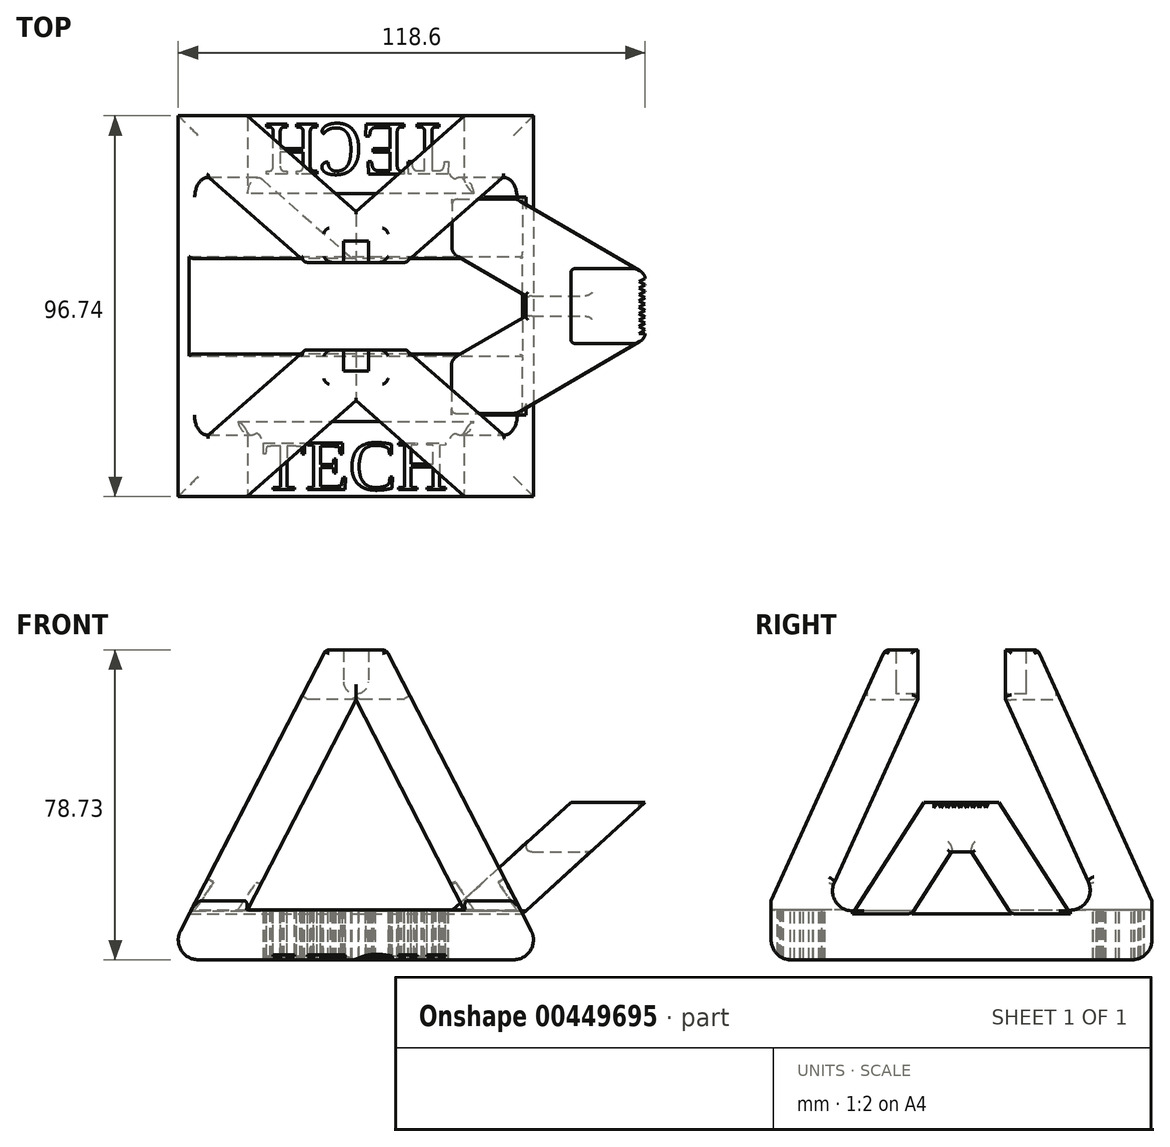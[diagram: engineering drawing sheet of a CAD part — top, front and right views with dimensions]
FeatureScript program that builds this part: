
annotation { "Feature Type Name" : "Feature", "Feature Type Description" : "" }
export const myFeature = defineFeature(function(context is Context, id is Id, definition is map)
    precondition{}
    {
        {
            var Q0;
            Q0=qCreatedBy(makeId("Front.planeOp"),FACE);
            var sketch = newSketch(context, id + "F0", { "sketchPlane" : qUnion([Q0])});
            skLineSegment(sketch, "E0", {"start": v(0, 54.73) * mm, "end": v(0, -72.39) * mm, "construction": true});
            skLineSegment(sketch, "E1", {"start": v(0, 35.91) * mm, "end": v(-7.58, 35.91) * mm});
            skLineSegment(sketch, "E2", {"start": v(-7.58, 35.91) * mm, "end": v(-48.37, -43.08) * mm});
            skLineSegment(sketch, "E3", {"start": v(-48.37, -43.08) * mm, "end": v(0, -43.08) * mm});
            skLineSegment(sketch, "E4", {"start": v(0, -43.08) * mm, "end": v(0, 35.91) * mm});
            skLineSegment(sketch, "E5.MirrorCS", {"start": v(7.58, 35.91) * mm, "end": v(48.37, -43.08) * mm});
            skLineSegment(sketch, "E6.MirrorCS", {"start": v(0, 35.91) * mm, "end": v(7.58, 35.91) * mm});
            skLineSegment(sketch, "E7.MirrorCS", {"start": v(48.37, -43.08) * mm, "end": v(0, -43.08) * mm});
            skSolve(sketch);
        }
        {
            var Q0;
            Q0=makeQuery(id+"F0.imprint","IMPRINT",FACE,{"disambiguationData":[TD([[makeQuery(id+"F0.imprint","IMPRINT",EDGE,{"derivedFrom":sQuery(id+"F0.wireOp",EDGE,"E1")}),1.0]])]});
            var Q1;
            Q1=makeQuery(id+"F0.imprint","IMPRINT",FACE,{"disambiguationData":[TD([[makeQuery(id+"F0.imprint","IMPRINT",EDGE,{"derivedFrom":sQuery(id+"F0.wireOp",EDGE,"E4")}),-1.0]])]});
            extrude(context, id + "F1", {"entities" : qUnion([Q0, Q1]), "endBound" : BoundingType.SYMMETRIC, "depth" : 96.75 * mm});
        }
        {
            var Q0;
            Q0=qCreatedBy(makeId("Right.planeOp"),FACE);
            cPlane(context, id + "F2", {"entities" : qUnion([Q0]), "cplaneType" : CPlaneType.OFFSET, "offset" : 48.37 * mm, "width" : 152.4 * mm, "height" : 152.4 * mm});
        }
        {
            var Q0;
            Q0=qCreatedBy(id+"F2.planeOp",FACE);
            var sketch = newSketch(context, id + "F3", { "sketchPlane" : qUnion([Q0])});
            skLineSegment(sketch, "E8.bottom", {"start": v(49.54, -43.11) * mm, "end": v(-49.54, -43.41) * mm});
            skLineSegment(sketch, "E8.left", {"start": v(49.54, -43.11) * mm, "end": v(49.54, 35.91) * mm});
            skLineSegment(sketch, "E8.right", {"start": v(-49.54, -43.41) * mm, "end": v(-49.54, 35.91) * mm});
            skPoint(sketch, "E8.middle", {"position": v(0, 0) * mm});
            skLineSegment(sketch, "E9", {"start": v(0, 43.26) * mm, "end": v(0, -59.7) * mm, "construction": true});
            skPoint(sketch, "E9.endSnap0", {"position": v(0, -43.26) * mm});
            skLineSegment(sketch, "E10.0", {"start": v(48.25, -30.42) * mm, "end": v(-35.6, -30.67) * mm});
            skLineSegment(sketch, "E11.0", {"start": v(-11.11, 35.91) * mm, "end": v(-11.11, 23.21) * mm});
            skLineSegment(sketch, "E12.0", {"start": v(-23.81, 35.91) * mm, "end": v(-23.81, 35.65) * mm});
            skLineSegment(sketch, "E13", {"start": v(-49.54, 35.91) * mm, "end": v(49.54, 35.91) * mm});
            skPoint(sketch, "E14.orphan", {"position": v(0, 61.2) * mm});
            skPoint(sketch, "E15.orphan", {"position": v(49.54, 43.41) * mm});
            skPoint(sketch, "E16.orphan", {"position": v(-49.54, 43.11) * mm});
            skLineSegment(sketch, "E17.0", {"start": v(-48.25, 35.65) * mm, "end": v(48.25, 35.65) * mm});
            skLineSegment(sketch, "E18", {"start": v(-11.11, 23.21) * mm, "end": v(-35.6, -30.67) * mm});
            skLineSegment(sketch, "E19.0", {"start": v(-19.41, 35.65) * mm, "end": v(-49.54, -30.65) * mm});
            skLineSegment(sketch, "E20.trimOffspring", {"start": v(-11.11, 23.21) * mm, "end": v(48.25, 23.21) * mm});
            skLineSegment(sketch, "E21.trimOffspring", {"start": v(-35.55, 35.65) * mm, "end": v(-35.55, 35.91) * mm});
            skLineSegment(sketch, "E22.trimOffspring", {"start": v(-23.81, -43.33) * mm, "end": v(-23.81, -59.7) * mm});
            skLineSegment(sketch, "E23.trimOffspring", {"start": v(-11.11, -43.3) * mm, "end": v(-11.11, -59.7) * mm});
            skLineSegment(sketch, "E24.MirrorCS", {"start": v(11.11, 35.91) * mm, "end": v(11.11, 23.21) * mm});
            skLineSegment(sketch, "E25.MirrorCS", {"start": v(19.41, 35.65) * mm, "end": v(49.54, -30.65) * mm});
            skLineSegment(sketch, "E26.MirrorCS", {"start": v(11.11, 23.21) * mm, "end": v(35.6, -30.67) * mm});
            skSolve(sketch);
        }
        {
            var Q0;
            {var subQ5=sQuery(id+"F3.wireOp",EDGE,"E21.trimOffspring");Q0=makeQuery(id+"F3.imprint","IMPRINT",FACE,{"disambiguationData":[TD([[makeQuery(id+"F3.imprint","IMPRINT",EDGE,{"derivedFrom":subQ5}),1.0]])]});}
            var Q1;
            {var subQ4=sQuery(id+"F3.wireOp",EDGE,"E13");var subQ5=sQuery(id+"F3.wireOp",EDGE,"E8.left");var subQ6=makeQuery(id+"F3.imprint","INTERSECT",VERTEX,{"derivedFrom":[subQ5,subQ4]});Q1=makeQuery(id+"F3.imprint","IMPRINT",FACE,{"disambiguationData":[TD([[makeQuery(id+"F3.imprint","IMPRINT",EDGE,{"disambiguationData":[TD([[subQ6,1.0]])],"derivedFrom":subQ5}),1.0]])]});}
            var Q2;
            {var subQ0=sQuery(id+"F3.wireOp",EDGE,"E13");var subQ1=sQuery(id+"F3.wireOp",EDGE,"E11.0");var subQ2=makeQuery(id+"F3.imprint","INTERSECT",VERTEX,{"derivedFrom":[subQ1,subQ0]});Q2=makeQuery(id+"F3.imprint","IMPRINT",FACE,{"disambiguationData":[TD([[makeQuery(id+"F3.imprint","IMPRINT",EDGE,{"disambiguationData":[TD([[subQ2,-1.0]])],"derivedFrom":subQ1}),1.0]])]});}
            var Q3;
            {var subQ0=sQuery(id+"F3.wireOp",EDGE,"E12.0");Q3=makeQuery(id+"F3.imprint","IMPRINT",FACE,{"disambiguationData":[TD([[makeQuery(id+"F3.imprint","IMPRINT",EDGE,{"derivedFrom":subQ0}),-1.0]])]});}
            var Q4;
            {var subQ0=sQuery(id+"F3.wireOp",EDGE,"E12.0");Q4=makeQuery(id+"F3.imprint","IMPRINT",FACE,{"disambiguationData":[TD([[makeQuery(id+"F3.imprint","IMPRINT",EDGE,{"derivedFrom":subQ0}),1.0]])]});}
            var Q5;
            {var subQ0=sQuery(id+"F3.wireOp",EDGE,"E17.0");var subQ1=sQuery(id+"F3.wireOp",EDGE,"E8.left");var subQ2=makeQuery(id+"F3.imprint","INTERSECT",VERTEX,{"derivedFrom":[subQ1,subQ0]});Q5=makeQuery(id+"F3.imprint","IMPRINT",FACE,{"disambiguationData":[TD([[makeQuery(id+"F3.imprint","IMPRINT",EDGE,{"disambiguationData":[TD([[subQ2,1.0]])],"derivedFrom":subQ1}),1.0]])]});}
            var Q6;
            {var subQ0=sQuery(id+"F3.wireOp",EDGE,"E20.trimOffspring");var subQ1=sQuery(id+"F3.wireOp",EDGE,"E8.left");var subQ2=makeQuery(id+"F3.imprint","INTERSECT",VERTEX,{"derivedFrom":[subQ1,subQ0]});Q6=makeQuery(id+"F3.imprint","IMPRINT",FACE,{"disambiguationData":[TD([[makeQuery(id+"F3.imprint","IMPRINT",EDGE,{"disambiguationData":[TD([[subQ2,1.0]])],"derivedFrom":subQ1}),1.0]])]});}
            var Q7;
            {var subQ1=sQuery(id+"F3.wireOp",EDGE,"E11.0");var subQ3=sQuery(id+"F3.wireOp",EDGE,"E17.0");var subQ4=makeQuery(id+"F3.imprint","INTERSECT",VERTEX,{"derivedFrom":[subQ1,subQ3]});Q7=makeQuery(id+"F3.imprint","IMPRINT",FACE,{"disambiguationData":[TD([[makeQuery(id+"F3.imprint","IMPRINT",EDGE,{"disambiguationData":[TD([[subQ4,-1.0]])],"derivedFrom":subQ3}),-1.0]])]});}
            var Q8;
            {var subQ0=sQuery(id+"F3.wireOp",EDGE,"E18");Q8=makeQuery(id+"F3.imprint","IMPRINT",FACE,{"disambiguationData":[TD([[makeQuery(id+"F3.imprint","IMPRINT",EDGE,{"derivedFrom":subQ0}),1.0]])]});}
            var Q9;
            {var subQ2=sQuery(id+"F3.wireOp",EDGE,"E19.0");Q9=makeQuery(id+"F3.imprint","IMPRINT",FACE,{"disambiguationData":[TD([[makeQuery(id+"F3.imprint","IMPRINT",EDGE,{"derivedFrom":subQ2}),-1.0]])]});}
            extrude(context, id + "F4", {"entities" : qUnion([Q0, Q1, Q2, Q3, Q4, Q5, Q6, Q7, Q8, Q9]), "operationType" : NewBodyOperationType.REMOVE, "endBound" : BoundingType.THROUGH_ALL, "oppositeDirection" : true, "depth" : 25.4 * mm});
        }
        {
            var Q0;
            Q0=makeQuery(id+"F1.opExtrude","CAP_FACE",FACE,{"disambiguationData":[OSD([sQuery(id+"F0.wireOp",EDGE,"E1"),sQuery(id+"F0.wireOp",EDGE,"E2"),sQuery(id+"F0.wireOp",EDGE,"E3"),sQuery(id+"F0.wireOp",EDGE,"E5.MirrorCS"),sQuery(id+"F0.wireOp",EDGE,"E6.MirrorCS"),sQuery(id+"F0.wireOp",EDGE,"E7.MirrorCS")])],"isStart":false});
            var sketch = newSketch(context, id + "F5", { "sketchPlane" : qUnion([Q0])});
            skLineSegment(sketch, "E27", {"start": v(-48.37, -43.08) * mm, "end": v(48.37, -43.08) * mm});
            skLineSegment(sketch, "E28.0", {"start": v(-48.37, -30.38) * mm, "end": v(48.37, -30.38) * mm});
            skLineSegment(sketch, "E29", {"start": v(-48.37, -43.08) * mm, "end": v(-7.72, 35.65) * mm});
            skLineSegment(sketch, "E30", {"start": v(-7.72, 35.65) * mm, "end": v(7.71, 35.65) * mm});
            skLineSegment(sketch, "E31", {"start": v(7.71, 35.65) * mm, "end": v(48.37, -43.08) * mm});
            skLineSegment(sketch, "E32.0", {"start": v(-37.1, -48.9) * mm, "end": v(3.57, 29.82) * mm});
            skLineSegment(sketch, "E33.0", {"start": v(-7.72, 22.95) * mm, "end": v(7.71, 22.95) * mm});
            skLineSegment(sketch, "E34.0", {"start": v(-3.57, 29.82) * mm, "end": v(37.1, -48.9) * mm});
            skSolve(sketch);
        }
        {
            var Q0;
            {var subQ0=sQuery(id+"F5.wireOp",EDGE,"E34.0");var subQ1=sQuery(id+"F5.wireOp",EDGE,"E32.0");var subQ2=makeQuery(id+"F5.imprint","INTERSECT",VERTEX,{"derivedFrom":[subQ1,subQ0]});Q0=makeQuery(id+"F5.imprint","IMPRINT",FACE,{"disambiguationData":[TD([[makeQuery(id+"F5.imprint","IMPRINT",EDGE,{"disambiguationData":[TD([[subQ2,1.0]])],"derivedFrom":subQ1}),-1.0]])]});}
            var Q1;
            {var subQ0=sQuery(id+"F5.wireOp",EDGE,"E32.0");var subQ1=sQuery(id+"F5.wireOp",EDGE,"E28.0");var subQ2=makeQuery(id+"F5.imprint","INTERSECT",VERTEX,{"derivedFrom":[subQ1,subQ0]});Q1=makeQuery(id+"F5.imprint","IMPRINT",FACE,{"disambiguationData":[TD([[makeQuery(id+"F5.imprint","IMPRINT",EDGE,{"disambiguationData":[TD([[subQ2,-1.0]])],"derivedFrom":subQ1}),1.0]])]});}
            extrude(context, id + "F6", {"entities" : qUnion([Q0, Q1]), "operationType" : NewBodyOperationType.REMOVE, "endBound" : BoundingType.THROUGH_ALL, "oppositeDirection" : true, "depth" : 25.4 * mm});
        }
        {
            var Q0;
            {var subQ0=sQuery(id+"F3.wireOp",EDGE,"E17.0");Q0=makeQuery(id+"F4.boolean.opBoolean","COPY",FACE,{"derivedFrom":makeQuery(id+"F4.opExtrude","SWEPT_FACE",FACE,{"disambiguationData":[OSD([subQ0]),TDD([makeQuery(id+"F3.imprint","IMPRINT",EDGE,{"disambiguationData":[TD([[makeQuery(id+"F3.imprint","INTERSECT",VERTEX,{"derivedFrom":[subQ0,sQuery(id+"F3.wireOp",EDGE,"E19.0")]}),-1.0]])],"derivedFrom":subQ0})])]})});}
            var sketch = newSketch(context, id + "F7", { "sketchPlane" : qUnion([Q0])});
            skLineSegment(sketch, "E35.bottom", {"start": v(-3.17, 16.51) * mm, "end": v(3.18, 16.51) * mm});
            skLineSegment(sketch, "E35.top", {"start": v(-3.18, -16.51) * mm, "end": v(3.17, -16.51) * mm});
            skLineSegment(sketch, "E35.left", {"start": v(-3.17, 16.51) * mm, "end": v(-3.18, -16.51) * mm});
            skLineSegment(sketch, "E35.right", {"start": v(3.18, 16.51) * mm, "end": v(3.17, -16.51) * mm});
            skPoint(sketch, "E35.middle", {"position": v(0, 0) * mm});
            skSolve(sketch);
        }
        {
            var Q0;
            Q0 = qSketchRegion(id + "F7", true);
            extrude(context, id + "F8", {"entities" : qUnion([Q0]), "operationType" : NewBodyOperationType.REMOVE, "oppositeDirection" : true, "depth" : 11.1 * mm});
        }
        {
            var Q0;
            {var subQ0=sQuery(id+"F7.wireOp",EDGE,"E35.left");Q0=makeQuery(id+"F8.boolean.opBoolean","COPY",EDGE,{"disambiguationData":[TD([makeQuery(id+"F4.boolean.opBoolean","COPY",FACE,{"derivedFrom":makeQuery(id+"F4.opExtrude","SWEPT_FACE",FACE,{"disambiguationData":[OSD([sQuery(id+"F3.wireOp",EDGE,"E11.0")])]})})])],"derivedFrom":makeQuery(id+"F8.opExtrude","CAP_EDGE",EDGE,{"disambiguationData":[OSD([subQ0])],"isStart":false})});}
            var Q1;
            {var subQ0=sQuery(id+"F7.wireOp",EDGE,"E35.right");Q1=makeQuery(id+"F8.boolean.opBoolean","COPY",EDGE,{"disambiguationData":[TD([makeQuery(id+"F4.boolean.opBoolean","COPY",FACE,{"derivedFrom":makeQuery(id+"F4.opExtrude","SWEPT_FACE",FACE,{"disambiguationData":[OSD([sQuery(id+"F3.wireOp",EDGE,"E11.0")])]})})])],"derivedFrom":makeQuery(id+"F8.opExtrude","CAP_EDGE",EDGE,{"disambiguationData":[OSD([subQ0])],"isStart":false})});}
            var Q2;
            {var subQ0=sQuery(id+"F7.wireOp",EDGE,"E35.left");Q2=makeQuery(id+"F8.boolean.opBoolean","COPY",EDGE,{"disambiguationData":[TD([makeQuery(id+"F4.boolean.opBoolean","COPY",FACE,{"derivedFrom":makeQuery(id+"F4.opExtrude","SWEPT_FACE",FACE,{"disambiguationData":[OSD([sQuery(id+"F3.wireOp",EDGE,"E24.MirrorCS")])]})})])],"derivedFrom":makeQuery(id+"F8.opExtrude","CAP_EDGE",EDGE,{"disambiguationData":[OSD([subQ0])],"isStart":false})});}
            var Q3;
            {var subQ1=sQuery(id+"F7.wireOp",EDGE,"E35.right");Q3=makeQuery(id+"F8.boolean.opBoolean","COPY",EDGE,{"disambiguationData":[TD([makeQuery(id+"F4.boolean.opBoolean","COPY",FACE,{"derivedFrom":makeQuery(id+"F4.opExtrude","SWEPT_FACE",FACE,{"disambiguationData":[OSD([sQuery(id+"F3.wireOp",EDGE,"E24.MirrorCS")])]})})])],"derivedFrom":makeQuery(id+"F8.opExtrude","CAP_EDGE",EDGE,{"disambiguationData":[OSD([subQ1])],"isStart":false})});}
            fillet(context, id + "F9", {"entities" : qUnion([Q0, Q1, Q2, Q3]), "radius" : 3.05 * mm, "tangentPropagation" : true, "allowEdgeOverflow" : false});
        }
        {
            var Q0;
            Q0=makeQuery(id+"F4.boolean.opBoolean","COPY",EDGE,{"derivedFrom":makeQuery(id+"F4.opExtrude","SWEPT_EDGE",EDGE,{"disambiguationData":[OSD([sQuery(id+"F3.wireOp",EDGE,"E10.0"),sQuery(id+"F3.wireOp",EDGE,"E18")])]})});
            var Q1;
            Q1=makeQuery(id+"F4.boolean.opBoolean","COPY",EDGE,{"derivedFrom":makeQuery(id+"F4.opExtrude","SWEPT_EDGE",EDGE,{"disambiguationData":[OSD([sQuery(id+"F3.wireOp",EDGE,"E10.0"),sQuery(id+"F3.wireOp",EDGE,"E26.MirrorCS")])]})});
            fillet(context, id + "F10", {"entities" : qUnion([Q0, Q1]), "radius" : 5.08 * mm, "tangentPropagation" : true, "allowEdgeOverflow" : false});
        }
        {
            var Q0;
            Q0=makeQuery(id+"F1.opExtrude","CAP_EDGE",EDGE,{"disambiguationData":[OSD([sQuery(id+"F0.wireOp",EDGE,"E3"),sQuery(id+"F0.wireOp",EDGE,"E7.MirrorCS")])],"isStart":true});
            var Q1;
            Q1=makeQuery(id+"F1.opExtrude","SWEPT_EDGE",EDGE,{"disambiguationData":[OSD([sQuery(id+"F0.wireOp",EDGE,"E2"),sQuery(id+"F0.wireOp",EDGE,"E3")])]});
            var Q2;
            Q2=makeQuery(id+"F1.opExtrude","SWEPT_EDGE",EDGE,{"disambiguationData":[OSD([sQuery(id+"F0.wireOp",EDGE,"E5.MirrorCS"),sQuery(id+"F0.wireOp",EDGE,"E7.MirrorCS")])]});
            var Q3;
            Q3=makeQuery(id+"F1.opExtrude","CAP_EDGE",EDGE,{"disambiguationData":[OSD([sQuery(id+"F0.wireOp",EDGE,"E3"),sQuery(id+"F0.wireOp",EDGE,"E7.MirrorCS")])],"isStart":false});
            fillet(context, id + "F11", {"entities" : qUnion([Q0, Q1, Q2, Q3]), "radius" : 5.08 * mm, "tangentPropagation" : true, "allowEdgeOverflow" : false});
        }
        {
            var Q0;
            Q0=makeQuery(id+"F6.boolean.opBoolean","INTERSECT",EDGE,{"derivedFrom":[makeQuery(id+"F4.boolean.opBoolean","COPY",FACE,{"derivedFrom":makeQuery(id+"F4.opExtrude","SWEPT_FACE",FACE,{"disambiguationData":[OSD([sQuery(id+"F3.wireOp",EDGE,"E25.MirrorCS")])]})}),makeQuery(id+"F6.opExtrude","SWEPT_FACE",FACE,{"disambiguationData":[OSD([sQuery(id+"F5.wireOp",EDGE,"E32.0")])]})]});
            var Q1;
            Q1=makeQuery(id+"F6.boolean.opBoolean","INTERSECT",EDGE,{"derivedFrom":[makeQuery(id+"F4.boolean.opBoolean","COPY",FACE,{"derivedFrom":makeQuery(id+"F4.opExtrude","SWEPT_FACE",FACE,{"disambiguationData":[OSD([sQuery(id+"F3.wireOp",EDGE,"E25.MirrorCS")])]})}),makeQuery(id+"F6.opExtrude","SWEPT_FACE",FACE,{"disambiguationData":[OSD([sQuery(id+"F5.wireOp",EDGE,"E34.0")])]})]});
            var Q2;
            Q2=makeQuery(id+"F4.boolean.opBoolean","INTERSECT",EDGE,{"derivedFrom":[makeQuery(id+"F1.opExtrude","SWEPT_FACE",FACE,{"disambiguationData":[OSD([sQuery(id+"F0.wireOp",EDGE,"E2")])]}),makeQuery(id+"F4.opExtrude","SWEPT_FACE",FACE,{"disambiguationData":[OSD([sQuery(id+"F3.wireOp",EDGE,"E25.MirrorCS")])]})]});
            var Q3;
            Q3=makeQuery(id+"F4.boolean.opBoolean","INTERSECT",EDGE,{"derivedFrom":[makeQuery(id+"F1.opExtrude","SWEPT_FACE",FACE,{"disambiguationData":[OSD([sQuery(id+"F0.wireOp",EDGE,"E2")])]}),makeQuery(id+"F4.opExtrude","SWEPT_FACE",FACE,{"disambiguationData":[OSD([sQuery(id+"F3.wireOp",EDGE,"E26.MirrorCS")])]})]});
            var Q4;
            Q4=makeQuery(id+"F4.boolean.opBoolean","INTERSECT",EDGE,{"derivedFrom":[makeQuery(id+"F1.opExtrude","SWEPT_FACE",FACE,{"disambiguationData":[OSD([sQuery(id+"F0.wireOp",EDGE,"E5.MirrorCS")])]}),makeQuery(id+"F4.opExtrude","SWEPT_FACE",FACE,{"disambiguationData":[OSD([sQuery(id+"F3.wireOp",EDGE,"E26.MirrorCS")])]})]});
            var Q5;
            Q5=makeQuery(id+"F6.boolean.opBoolean","INTERSECT",EDGE,{"derivedFrom":[makeQuery(id+"F4.boolean.opBoolean","COPY",FACE,{"derivedFrom":makeQuery(id+"F4.opExtrude","SWEPT_FACE",FACE,{"disambiguationData":[OSD([sQuery(id+"F3.wireOp",EDGE,"E26.MirrorCS")])]})}),makeQuery(id+"F6.opExtrude","SWEPT_FACE",FACE,{"disambiguationData":[OSD([sQuery(id+"F5.wireOp",EDGE,"E34.0")])]})]});
            var Q6;
            Q6=makeQuery(id+"F6.boolean.opBoolean","INTERSECT",EDGE,{"derivedFrom":[makeQuery(id+"F4.boolean.opBoolean","COPY",FACE,{"derivedFrom":makeQuery(id+"F4.opExtrude","SWEPT_FACE",FACE,{"disambiguationData":[OSD([sQuery(id+"F3.wireOp",EDGE,"E19.0")])]})}),makeQuery(id+"F6.opExtrude","SWEPT_FACE",FACE,{"disambiguationData":[OSD([sQuery(id+"F5.wireOp",EDGE,"E34.0")])]})]});
            var Q7;
            Q7=makeQuery(id+"F6.boolean.opBoolean","INTERSECT",EDGE,{"derivedFrom":[makeQuery(id+"F4.boolean.opBoolean","COPY",FACE,{"derivedFrom":makeQuery(id+"F4.opExtrude","SWEPT_FACE",FACE,{"disambiguationData":[OSD([sQuery(id+"F3.wireOp",EDGE,"E19.0")])]})}),makeQuery(id+"F6.opExtrude","SWEPT_FACE",FACE,{"disambiguationData":[OSD([sQuery(id+"F5.wireOp",EDGE,"E32.0")])]})]});
            var Q8;
            Q8=makeQuery(id+"F6.boolean.opBoolean","INTERSECT",EDGE,{"derivedFrom":[makeQuery(id+"F4.boolean.opBoolean","COPY",FACE,{"derivedFrom":makeQuery(id+"F4.opExtrude","SWEPT_FACE",FACE,{"disambiguationData":[OSD([sQuery(id+"F3.wireOp",EDGE,"E18")])]})}),makeQuery(id+"F6.opExtrude","SWEPT_FACE",FACE,{"disambiguationData":[OSD([sQuery(id+"F5.wireOp",EDGE,"E32.0")])]})]});
            var Q9;
            Q9=makeQuery(id+"F6.boolean.opBoolean","INTERSECT",EDGE,{"derivedFrom":[makeQuery(id+"F4.boolean.opBoolean","COPY",FACE,{"derivedFrom":makeQuery(id+"F4.opExtrude","SWEPT_FACE",FACE,{"disambiguationData":[OSD([sQuery(id+"F3.wireOp",EDGE,"E18")])]})}),makeQuery(id+"F6.opExtrude","SWEPT_FACE",FACE,{"disambiguationData":[OSD([sQuery(id+"F5.wireOp",EDGE,"E34.0")])]})]});
            var Q10;
            Q10=makeQuery(id+"F4.boolean.opBoolean","INTERSECT",EDGE,{"derivedFrom":[makeQuery(id+"F1.opExtrude","SWEPT_FACE",FACE,{"disambiguationData":[OSD([sQuery(id+"F0.wireOp",EDGE,"E2")])]}),makeQuery(id+"F4.opExtrude","SWEPT_FACE",FACE,{"disambiguationData":[OSD([sQuery(id+"F3.wireOp",EDGE,"E24.MirrorCS")])]})]});
            var Q11;
            Q11=makeQuery(id+"F4.boolean.opBoolean","INTERSECT",EDGE,{"derivedFrom":[makeQuery(id+"F1.opExtrude","SWEPT_FACE",FACE,{"disambiguationData":[OSD([sQuery(id+"F0.wireOp",EDGE,"E2")])]}),makeQuery(id+"F4.opExtrude","SWEPT_FACE",FACE,{"disambiguationData":[OSD([sQuery(id+"F3.wireOp",EDGE,"E11.0")])]})]});
            var Q12;
            Q12=makeQuery(id+"F4.boolean.opBoolean","COPY",EDGE,{"derivedFrom":makeQuery(id+"F4.opExtrude","SWEPT_EDGE",EDGE,{"disambiguationData":[OSD([sQuery(id+"F3.wireOp",EDGE,"E17.0"),sQuery(id+"F3.wireOp",EDGE,"E25.MirrorCS")])]})});
            var Q13;
            {var subQ0=sQuery(id+"F3.wireOp",EDGE,"E17.0");Q13=makeQuery(id+"F4.boolean.opBoolean","INTERSECT",EDGE,{"derivedFrom":[makeQuery(id+"F1.opExtrude","SWEPT_FACE",FACE,{"disambiguationData":[OSD([sQuery(id+"F0.wireOp",EDGE,"E5.MirrorCS")])]}),makeQuery(id+"F4.opExtrude","SWEPT_FACE",FACE,{"disambiguationData":[OSD([subQ0]),TDD([makeQuery(id+"F3.imprint","IMPRINT",EDGE,{"disambiguationData":[TD([[makeQuery(id+"F3.imprint","INTERSECT",VERTEX,{"derivedFrom":[subQ0,sQuery(id+"F3.wireOp",EDGE,"E25.MirrorCS")]}),1.0]])],"derivedFrom":subQ0})])]})]});}
            var Q14;
            {var subQ0=sQuery(id+"F3.wireOp",EDGE,"E17.0");Q14=makeQuery(id+"F4.boolean.opBoolean","INTERSECT",EDGE,{"derivedFrom":[makeQuery(id+"F1.opExtrude","SWEPT_FACE",FACE,{"disambiguationData":[OSD([sQuery(id+"F0.wireOp",EDGE,"E2")])]}),makeQuery(id+"F4.opExtrude","SWEPT_FACE",FACE,{"disambiguationData":[OSD([subQ0]),TDD([makeQuery(id+"F3.imprint","IMPRINT",EDGE,{"disambiguationData":[TD([[makeQuery(id+"F3.imprint","INTERSECT",VERTEX,{"derivedFrom":[subQ0,sQuery(id+"F3.wireOp",EDGE,"E25.MirrorCS")]}),1.0]])],"derivedFrom":subQ0})])]})]});}
            var Q15;
            Q15=makeQuery(id+"F4.boolean.opBoolean","INTERSECT",EDGE,{"derivedFrom":[makeQuery(id+"F1.opExtrude","SWEPT_FACE",FACE,{"disambiguationData":[OSD([sQuery(id+"F0.wireOp",EDGE,"E5.MirrorCS")])]}),makeQuery(id+"F4.opExtrude","SWEPT_FACE",FACE,{"disambiguationData":[OSD([sQuery(id+"F3.wireOp",EDGE,"E24.MirrorCS")])]})]});
            var Q16;
            Q16=makeQuery(id+"F4.boolean.opBoolean","INTERSECT",EDGE,{"derivedFrom":[makeQuery(id+"F1.opExtrude","SWEPT_FACE",FACE,{"disambiguationData":[OSD([sQuery(id+"F0.wireOp",EDGE,"E5.MirrorCS")])]}),makeQuery(id+"F4.opExtrude","SWEPT_FACE",FACE,{"disambiguationData":[OSD([sQuery(id+"F3.wireOp",EDGE,"E25.MirrorCS")])]})]});
            var Q17;
            Q17=makeQuery(id+"F4.boolean.opBoolean","INTERSECT",EDGE,{"derivedFrom":[makeQuery(id+"F1.opExtrude","SWEPT_FACE",FACE,{"disambiguationData":[OSD([sQuery(id+"F0.wireOp",EDGE,"E2")])]}),makeQuery(id+"F4.opExtrude","SWEPT_FACE",FACE,{"disambiguationData":[OSD([sQuery(id+"F3.wireOp",EDGE,"E19.0")])]})]});
            var Q18;
            Q18=makeQuery(id+"F4.boolean.opBoolean","INTERSECT",EDGE,{"derivedFrom":[makeQuery(id+"F1.opExtrude","SWEPT_FACE",FACE,{"disambiguationData":[OSD([sQuery(id+"F0.wireOp",EDGE,"E5.MirrorCS")])]}),makeQuery(id+"F4.opExtrude","SWEPT_FACE",FACE,{"disambiguationData":[OSD([sQuery(id+"F3.wireOp",EDGE,"E19.0")])]})]});
            var Q19;
            {var subQ0=sQuery(id+"F3.wireOp",EDGE,"E17.0");Q19=makeQuery(id+"F4.boolean.opBoolean","INTERSECT",EDGE,{"derivedFrom":[makeQuery(id+"F1.opExtrude","SWEPT_FACE",FACE,{"disambiguationData":[OSD([sQuery(id+"F0.wireOp",EDGE,"E2")])]}),makeQuery(id+"F4.opExtrude","SWEPT_FACE",FACE,{"disambiguationData":[OSD([subQ0]),TDD([makeQuery(id+"F3.imprint","IMPRINT",EDGE,{"disambiguationData":[TD([[makeQuery(id+"F3.imprint","INTERSECT",VERTEX,{"derivedFrom":[subQ0,sQuery(id+"F3.wireOp",EDGE,"E19.0")]}),-1.0]])],"derivedFrom":subQ0})])]})]});}
            var Q20;
            Q20=makeQuery(id+"F4.boolean.opBoolean","COPY",EDGE,{"derivedFrom":makeQuery(id+"F4.opExtrude","SWEPT_EDGE",EDGE,{"disambiguationData":[OSD([sQuery(id+"F3.wireOp",EDGE,"E17.0"),sQuery(id+"F3.wireOp",EDGE,"E19.0")])]})});
            var Q21;
            {var subQ0=sQuery(id+"F3.wireOp",EDGE,"E17.0");Q21=makeQuery(id+"F4.boolean.opBoolean","INTERSECT",EDGE,{"derivedFrom":[makeQuery(id+"F1.opExtrude","SWEPT_FACE",FACE,{"disambiguationData":[OSD([sQuery(id+"F0.wireOp",EDGE,"E5.MirrorCS")])]}),makeQuery(id+"F4.opExtrude","SWEPT_FACE",FACE,{"disambiguationData":[OSD([subQ0]),TDD([makeQuery(id+"F3.imprint","IMPRINT",EDGE,{"disambiguationData":[TD([[makeQuery(id+"F3.imprint","INTERSECT",VERTEX,{"derivedFrom":[subQ0,sQuery(id+"F3.wireOp",EDGE,"E19.0")]}),-1.0]])],"derivedFrom":subQ0})])]})]});}
            var Q22;
            Q22=makeQuery(id+"F4.boolean.opBoolean","INTERSECT",EDGE,{"derivedFrom":[makeQuery(id+"F1.opExtrude","SWEPT_FACE",FACE,{"disambiguationData":[OSD([sQuery(id+"F0.wireOp",EDGE,"E5.MirrorCS")])]}),makeQuery(id+"F4.opExtrude","SWEPT_FACE",FACE,{"disambiguationData":[OSD([sQuery(id+"F3.wireOp",EDGE,"E11.0")])]})]});
            fillet(context, id + "F12", {"entities" : qUnion([Q0, Q1, Q2, Q3, Q4, Q5, Q6, Q7, Q8, Q9, Q10, Q11, Q12, Q13, Q14, Q15, Q16, Q17, Q18, Q19, Q20, Q21, Q22]), "radius" : 1.52 * mm, "tangentPropagation" : true, "allowEdgeOverflow" : false});
        }
        {
            var Q0;
            Q0=makeQuery(id+"F6.boolean.opBoolean","COPY",FACE,{"disambiguationData":[TD([makeQuery(id+"F4.boolean.opBoolean","COPY",FACE,{"derivedFrom":makeQuery(id+"F4.opExtrude","SWEPT_FACE",FACE,{"disambiguationData":[OSD([sQuery(id+"F3.wireOp",EDGE,"E18")])]})})])],"derivedFrom":makeQuery(id+"F6.opExtrude","SWEPT_FACE",FACE,{"disambiguationData":[OSD([sQuery(id+"F5.wireOp",EDGE,"E28.0")])]})});
            var sketch = newSketch(context, id + "F13", { "sketchPlane" : qUnion([Q0])});
            skText(sketch, "E36", { "text": "TECH", "fontName": "Tinos-Regular.ttf"});
            skText(sketch, "E37", { "text": "TECH", "fontName": "NotoSerif-Regular.ttf"});
            const initialGuessF13  = {"E36": [-0.0238, -0.04662, 1, 0, 0.013], "E37": [0.02384, 0.04628, -1, 0, 0.01287]};
            skSetInitialGuess(sketch, initialGuessF13);
            skSolve(sketch);
        }
        {
            var Q0;
            Q0=makeQuery(id+"F13.imprint","IMPRINT",FACE,{"disambiguationData":[TD([[makeQuery(id+"F13.imprint","IMPRINT",EDGE,{"derivedFrom":sQuery(id+"F13.wireOp",EDGE,"E37.sketch_text.stroke-0")}),-1.0]])]});
            var Q1;
            Q1=makeQuery(id+"F13.imprint","IMPRINT",FACE,{"disambiguationData":[TD([[makeQuery(id+"F13.imprint","IMPRINT",EDGE,{"derivedFrom":sQuery(id+"F13.wireOp",EDGE,"E37.sketch_text.stroke-32")}),-1.0]])]});
            var Q2;
            Q2=makeQuery(id+"F13.imprint","IMPRINT",FACE,{"disambiguationData":[TD([[makeQuery(id+"F13.imprint","IMPRINT",EDGE,{"derivedFrom":sQuery(id+"F13.wireOp",EDGE,"E37.sketch_text.stroke-68")}),-1.0]])]});
            var Q3;
            Q3=makeQuery(id+"F13.imprint","IMPRINT",FACE,{"disambiguationData":[TD([[makeQuery(id+"F13.imprint","IMPRINT",EDGE,{"derivedFrom":sQuery(id+"F13.wireOp",EDGE,"E37.sketch_text.stroke-106")}),-1.0]])]});
            var Q4;
            Q4=makeQuery(id+"F13.imprint","IMPRINT",FACE,{"disambiguationData":[TD([[makeQuery(id+"F13.imprint","IMPRINT",EDGE,{"derivedFrom":sQuery(id+"F13.wireOp",EDGE,"E36.sketch_text.stroke-65")}),-1.0]])]});
            var Q5;
            Q5=makeQuery(id+"F13.imprint","IMPRINT",FACE,{"disambiguationData":[TD([[makeQuery(id+"F13.imprint","IMPRINT",EDGE,{"derivedFrom":sQuery(id+"F13.wireOp",EDGE,"E36.sketch_text.stroke-0")}),-1.0]])]});
            var Q6;
            Q6=makeQuery(id+"F13.imprint","IMPRINT",FACE,{"disambiguationData":[TD([[makeQuery(id+"F13.imprint","IMPRINT",EDGE,{"derivedFrom":sQuery(id+"F13.wireOp",EDGE,"E36.sketch_text.stroke-19")}),-1.0]])]});
            var Q7;
            Q7=makeQuery(id+"F13.imprint","IMPRINT",FACE,{"disambiguationData":[TD([[makeQuery(id+"F13.imprint","IMPRINT",EDGE,{"derivedFrom":sQuery(id+"F13.wireOp",EDGE,"E36.sketch_text.stroke-45")}),-1.0]])]});
            extrude(context, id + "F14", {"entities" : qUnion([Q0, Q1, Q2, Q3, Q4, Q5, Q6, Q7]), "operationType" : NewBodyOperationType.REMOVE, "endBound" : BoundingType.THROUGH_ALL, "oppositeDirection" : true, "depth" : 25.4 * mm});
        }
        {
            var Q0;
            Q0=qCreatedBy(makeId("Front.planeOp"),FACE);
            var sketch = newSketch(context, id + "F15", { "sketchPlane" : qUnion([Q0])});
            skLineSegment(sketch, "E38", {"start": v(22.83, -31.99) * mm, "end": v(41.74, -31.99) * mm});
            skLineSegment(sketch, "E39", {"start": v(41.74, -31.99) * mm, "end": v(41.74, 5.64) * mm, "construction": true});
            skLineSegment(sketch, "E40.MirrorCS", {"start": v(41.7, -31.99) * mm, "end": v(73.5, -3.04) * mm});
            skPoint(sketch, "E41.orphan", {"position": v(40.1, -33.44) * mm});
            skLineSegment(sketch, "E42.0", {"start": v(22.83, -31.99) * mm, "end": v(59.91, 1.77) * mm});
            skLineSegment(sketch, "E43", {"start": v(73.5, -3.04) * mm, "end": v(54.63, -3.04) * mm});
            skLineSegment(sketch, "E44", {"start": v(41.74, -31.99) * mm, "end": v(41.7, -31.99) * mm});
            skSolve(sketch);
        }
        {
            var Q0;
            {var subQ2=sQuery(id+"F15.wireOp",EDGE,"E38");Q0=makeQuery(id+"F15.imprint","IMPRINT",FACE,{"disambiguationData":[TD([[makeQuery(id+"F15.imprint","IMPRINT",EDGE,{"derivedFrom":subQ2}),1.0]])]});}
            extrude(context, id + "F16", {"entities" : qUnion([Q0]), "operationType" : NewBodyOperationType.ADD, "endBound" : BoundingType.SYMMETRIC, "depth" : 55.32 * mm});
        }
        {
            var Q0;
            Q0=qCreatedBy(id+"F2.planeOp",FACE);
            cPlane(context, id + "F17", {"entities" : qUnion([Q0]), "cplaneType" : CPlaneType.OFFSET, "offset" : 25.4 * mm, "width" : 152.4 * mm, "height" : 152.4 * mm});
        }
        {
            var Q0;
            Q0=qCreatedBy(id+"F17.planeOp",FACE);
            var sketch = newSketch(context, id + "F18", { "sketchPlane" : qUnion([Q0])});
            skLineSegment(sketch, "E45.bottom", {"start": v(-27.72, -2.98) * mm, "end": v(27.7, -2.98) * mm});
            skLineSegment(sketch, "E45.top", {"start": v(-27.72, -31.4) * mm, "end": v(27.7, -31.4) * mm});
            skLineSegment(sketch, "E45.left", {"start": v(-27.72, -2.98) * mm, "end": v(-27.72, -31.4) * mm});
            skLineSegment(sketch, "E45.right", {"start": v(27.7, -2.98) * mm, "end": v(27.7, -31.4) * mm});
            skLineSegment(sketch, "E46", {"start": v(0, 0) * mm, "end": v(0, -49.78) * mm, "construction": true});
            skLineSegment(sketch, "E47.0", {"start": v(9.52, 0) * mm, "end": v(9.53, -49.78) * mm});
            skLineSegment(sketch, "E48.0", {"start": v(-9.53, 0) * mm, "end": v(-9.52, -49.78) * mm});
            skLineSegment(sketch, "E49", {"start": v(-27.72, -31.4) * mm, "end": v(-9.52, -2.98) * mm});
            skLineSegment(sketch, "E50", {"start": v(27.7, -31.4) * mm, "end": v(9.52, -2.98) * mm});
            skLineSegment(sketch, "E51.0", {"start": v(-17.03, -38.25) * mm, "end": v(-2.58, -15.68) * mm});
            skLineSegment(sketch, "E52.0", {"start": v(17, -38.24) * mm, "end": v(2.57, -15.68) * mm});
            skLineSegment(sketch, "E53.trimOffspring", {"start": v(0, -11.65) * mm, "end": v(1.17, -9.82) * mm});
            skLineSegment(sketch, "E54.trimOffspring", {"start": v(0, -11.65) * mm, "end": v(-1.17, -9.82) * mm});
            skLineSegment(sketch, "E55.trimOffspring", {"start": v(-2.58, -15.68) * mm, "end": v(2.57, -15.68) * mm});
            skLineSegment(sketch, "E56.trimOffspring", {"start": v(15, -15.68) * mm, "end": v(17.65, -15.68) * mm});
            skSolve(sketch);
        }
        {
            var Q0;
            {var subQ0=sQuery(id+"F18.wireOp",EDGE,"E51.0");var subQ1=sQuery(id+"F18.wireOp",EDGE,"E45.top");var subQ2=makeQuery(id+"F18.imprint","INTERSECT",VERTEX,{"derivedFrom":[subQ1,subQ0]});Q0=makeQuery(id+"F18.imprint","IMPRINT",FACE,{"disambiguationData":[TD([[makeQuery(id+"F18.imprint","IMPRINT",EDGE,{"disambiguationData":[TD([[subQ2,-1.0]])],"derivedFrom":subQ1}),1.0]])]});}
            var Q1;
            {var subQ0=sQuery(id+"F18.wireOp",EDGE,"E55.trimOffspring");Q1=makeQuery(id+"F18.imprint","IMPRINT",FACE,{"disambiguationData":[TD([[makeQuery(id+"F18.imprint","IMPRINT",EDGE,{"derivedFrom":subQ0}),-1.0]])]});}
            var Q2;
            {var subQ0=sQuery(id+"F18.wireOp",EDGE,"E47.0");var subQ1=sQuery(id+"F18.wireOp",EDGE,"E45.top");var subQ2=makeQuery(id+"F18.imprint","INTERSECT",VERTEX,{"derivedFrom":[subQ1,subQ0]});Q2=makeQuery(id+"F18.imprint","IMPRINT",FACE,{"disambiguationData":[TD([[makeQuery(id+"F18.imprint","IMPRINT",EDGE,{"disambiguationData":[TD([[subQ2,-1.0]])],"derivedFrom":subQ1}),1.0]])]});}
            extrude(context, id + "F19", {"entities" : qUnion([Q0, Q1, Q2]), "operationType" : NewBodyOperationType.REMOVE, "endBound" : BoundingType.THROUGH_ALL, "oppositeDirection" : true, "depth" : 25.4 * mm});
        }
        {
            var Q0;
            Q0=qCreatedBy(makeId("Right.planeOp"),FACE);
            cPlane(context, id + "F20", {"entities" : qUnion([Q0]), "cplaneType" : CPlaneType.OFFSET, "offset" : 32.5 * mm, "width" : 152.4 * mm, "height" : 152.4 * mm});
        }
        {
            var Q0;
            Q0=qCreatedBy(id+"F20.planeOp",FACE);
            var sketch = newSketch(context, id + "F21", { "sketchPlane" : qUnion([Q0])});
            skLineSegment(sketch, "E57.bottom", {"start": v(27.66, -30.64) * mm, "end": v(-27.67, -30.64) * mm});
            skLineSegment(sketch, "E57.top", {"start": v(27.66, -3) * mm, "end": v(-27.67, -3) * mm});
            skLineSegment(sketch, "E57.left", {"start": v(27.66, -30.64) * mm, "end": v(27.66, -3) * mm});
            skLineSegment(sketch, "E57.right", {"start": v(-27.67, -30.64) * mm, "end": v(-27.67, -3) * mm});
            skLineSegment(sketch, "E58", {"start": v(12.14, -30.64) * mm, "end": v(2.56, -15.67) * mm});
            skLineSegment(sketch, "E59", {"start": v(2.56, -15.67) * mm, "end": v(-2.58, -15.67) * mm});
            skLineSegment(sketch, "E60", {"start": v(-2.58, -15.67) * mm, "end": v(-12.15, -30.6) * mm});
            skLineSegment(sketch, "E61.0", {"start": v(27.22, -30.64) * mm, "end": v(9.53, -3) * mm});
            skLineSegment(sketch, "E62.0", {"start": v(-9.55, -3) * mm, "end": v(-27.26, -30.64) * mm});
            skSolve(sketch);
        }
        {
            var Q0;
            {var subQ0=sQuery(id+"F21.wireOp",EDGE,"E57.left");Q0=makeQuery(id+"F21.imprint","IMPRINT",FACE,{"disambiguationData":[TD([[makeQuery(id+"F21.imprint","IMPRINT",EDGE,{"derivedFrom":subQ0}),1.0]])]});}
            var Q1;
            {var subQ0=sQuery(id+"F21.wireOp",EDGE,"E57.right");Q1=makeQuery(id+"F21.imprint","IMPRINT",FACE,{"disambiguationData":[TD([[makeQuery(id+"F21.imprint","IMPRINT",EDGE,{"derivedFrom":subQ0}),-1.0]])]});}
            extrude(context, id + "F22", {"entities" : qUnion([Q0, Q1]), "operationType" : NewBodyOperationType.REMOVE, "depth" : 51.3 * mm});
        }
        {
            var Q0;
            Q0=makeQuery(id+"F22.boolean.opBoolean","COPY",FACE,{"derivedFrom":makeQuery(id+"F22.opExtrude","CAP_FACE",FACE,{"disambiguationData":[OSD([sQuery(id+"F21.wireOp",EDGE,"E57.bottom"),sQuery(id+"F21.wireOp",EDGE,"E57.top"),sQuery(id+"F21.wireOp",EDGE,"E57.left"),sQuery(id+"F21.wireOp",EDGE,"E61.0")])],"isStart":true})});
            var sketch = newSketch(context, id + "F23", { "sketchPlane" : qUnion([Q0])});
            skLineSegment(sketch, "E63", {"start": v(-27.26, -30.64) * mm, "end": v(-27.66, -30.64) * mm});
            skLineSegment(sketch, "E64", {"start": v(-27.66, -30.64) * mm, "end": v(-27.66, -23.17) * mm});
            skLineSegment(sketch, "E65", {"start": v(-27.66, -23.17) * mm, "end": v(-22.48, -23.17) * mm});
            skLineSegment(sketch, "E66", {"start": v(-22.48, -23.17) * mm, "end": v(-27.26, -30.64) * mm});
            skLineSegment(sketch, "E67", {"start": v(22.44, -23.17) * mm, "end": v(27.66, -23.17) * mm});
            skLineSegment(sketch, "E68", {"start": v(27.66, -23.17) * mm, "end": v(27.66, -30.48) * mm});
            skLineSegment(sketch, "E69", {"start": v(27.66, -30.48) * mm, "end": v(27.12, -30.48) * mm});
            skLineSegment(sketch, "E70", {"start": v(27.12, -30.48) * mm, "end": v(22.44, -23.17) * mm});
            skSolve(sketch);
        }
        {
            var Q0;
            Q0=makeQuery(id+"F23.imprint","IMPRINT",FACE,{"disambiguationData":[TD([[makeQuery(id+"F23.imprint","IMPRINT",EDGE,{"derivedFrom":sQuery(id+"F23.wireOp",EDGE,"E63")}),-1.0]])]});
            var Q1;
            Q1=makeQuery(id+"F23.imprint","IMPRINT",FACE,{"disambiguationData":[TD([[makeQuery(id+"F23.imprint","IMPRINT",EDGE,{"derivedFrom":sQuery(id+"F23.wireOp",EDGE,"E67")}),-1.0]])]});
            extrude(context, id + "F24", {"entities" : qUnion([Q0, Q1]), "operationType" : NewBodyOperationType.REMOVE, "oppositeDirection" : true, "depth" : 8.6 * mm});
        }
        {
            var Q0;
            Q0=makeQuery(id+"F22.boolean.opBoolean","INTERSECT",EDGE,{"derivedFrom":[makeQuery(id+"F16.opExtrude","SWEPT_FACE",FACE,{"disambiguationData":[OSD([sQuery(id+"F15.wireOp",EDGE,"E40.MirrorCS")])]}),makeQuery(id+"F22.opExtrude","SWEPT_FACE",FACE,{"disambiguationData":[OSD([sQuery(id+"F21.wireOp",EDGE,"E62.0")])]})]});
            var Q1;
            Q1=makeQuery(id+"F19.boolean.opBoolean","INTERSECT",EDGE,{"derivedFrom":[makeQuery(id+"F16.opExtrude","SWEPT_FACE",FACE,{"disambiguationData":[OSD([sQuery(id+"F15.wireOp",EDGE,"E40.MirrorCS")])]}),makeQuery(id+"F19.opExtrude","SWEPT_FACE",FACE,{"disambiguationData":[OSD([sQuery(id+"F18.wireOp",EDGE,"E52.0")])]})]});
            var Q2;
            Q2=makeQuery(id+"F19.boolean.opBoolean","INTERSECT",EDGE,{"derivedFrom":[makeQuery(id+"F16.opExtrude","SWEPT_FACE",FACE,{"disambiguationData":[OSD([sQuery(id+"F15.wireOp",EDGE,"E40.MirrorCS")])]}),makeQuery(id+"F19.opExtrude","SWEPT_FACE",FACE,{"disambiguationData":[OSD([sQuery(id+"F18.wireOp",EDGE,"E55.trimOffspring")])]})]});
            var Q3;
            Q3=makeQuery(id+"F19.boolean.opBoolean","INTERSECT",EDGE,{"derivedFrom":[makeQuery(id+"F16.opExtrude","SWEPT_FACE",FACE,{"disambiguationData":[OSD([sQuery(id+"F15.wireOp",EDGE,"E40.MirrorCS")])]}),makeQuery(id+"F19.opExtrude","SWEPT_FACE",FACE,{"disambiguationData":[OSD([sQuery(id+"F18.wireOp",EDGE,"E51.0")])]})]});
            var Q4;
            Q4=makeQuery(id+"F24.boolean.opBoolean","INTERSECT",EDGE,{"derivedFrom":[makeQuery(id+"F16.opExtrude","SWEPT_FACE",FACE,{"disambiguationData":[OSD([sQuery(id+"F15.wireOp",EDGE,"E42.0")])]}),makeQuery(id+"F24.opExtrude","SWEPT_FACE",FACE,{"disambiguationData":[OSD([sQuery(id+"F23.wireOp",EDGE,"E70")])]})]});
            var Q5;
            Q5=makeQuery(id+"F19.boolean.opBoolean","INTERSECT",EDGE,{"derivedFrom":[makeQuery(id+"F16.opExtrude","SWEPT_FACE",FACE,{"disambiguationData":[OSD([sQuery(id+"F15.wireOp",EDGE,"E42.0")])]}),makeQuery(id+"F19.opExtrude","SWEPT_FACE",FACE,{"disambiguationData":[OSD([sQuery(id+"F18.wireOp",EDGE,"E51.0")])]})]});
            var Q6;
            Q6=makeQuery(id+"F19.boolean.opBoolean","INTERSECT",EDGE,{"derivedFrom":[makeQuery(id+"F16.opExtrude","SWEPT_FACE",FACE,{"disambiguationData":[OSD([sQuery(id+"F15.wireOp",EDGE,"E42.0")])]}),makeQuery(id+"F19.opExtrude","SWEPT_FACE",FACE,{"disambiguationData":[OSD([sQuery(id+"F18.wireOp",EDGE,"E55.trimOffspring")])]})]});
            var Q7;
            Q7=makeQuery(id+"F19.boolean.opBoolean","INTERSECT",EDGE,{"derivedFrom":[makeQuery(id+"F16.opExtrude","SWEPT_FACE",FACE,{"disambiguationData":[OSD([sQuery(id+"F15.wireOp",EDGE,"E42.0")])]}),makeQuery(id+"F19.opExtrude","SWEPT_FACE",FACE,{"disambiguationData":[OSD([sQuery(id+"F18.wireOp",EDGE,"E52.0")])]})]});
            var Q8;
            Q8=makeQuery(id+"F22.boolean.opBoolean","INTERSECT",EDGE,{"derivedFrom":[makeQuery(id+"F16.opExtrude","SWEPT_FACE",FACE,{"disambiguationData":[OSD([sQuery(id+"F15.wireOp",EDGE,"E42.0")])]}),makeQuery(id+"F22.opExtrude","SWEPT_FACE",FACE,{"disambiguationData":[OSD([sQuery(id+"F21.wireOp",EDGE,"E62.0")])]})]});
            var Q9;
            Q9=makeQuery(id+"F22.boolean.opBoolean","INTERSECT",EDGE,{"derivedFrom":[makeQuery(id+"F16.opExtrude","SWEPT_FACE",FACE,{"disambiguationData":[OSD([sQuery(id+"F15.wireOp",EDGE,"E40.MirrorCS")])]}),makeQuery(id+"F22.opExtrude","SWEPT_FACE",FACE,{"disambiguationData":[OSD([sQuery(id+"F21.wireOp",EDGE,"E61.0")])]})]});
            fillet(context, id + "F25", {"entities" : qUnion([Q0, Q1, Q2, Q3, Q4, Q5, Q6, Q7, Q8, Q9]), "radius" : 1.52 * mm, "tangentPropagation" : true, "allowEdgeOverflow" : false});
        }
        {
            var Q0;
            Q0=makeQuery(id+"F16.opExtrude","SWEPT_FACE",FACE,{"disambiguationData":[OSD([sQuery(id+"F15.wireOp",EDGE,"E43")])]});
            var sketch = newSketch(context, id + "F26", { "sketchPlane" : qUnion([Q0])});
            skLineSegment(sketch, "E71.bottom", {"start": v(73.5, 7.02) * mm, "end": v(71.92, 7.02) * mm});
            skLineSegment(sketch, "E71.top", {"start": v(73.5, -7.04) * mm, "end": v(71.92, -7.04) * mm});
            skLineSegment(sketch, "E71.left", {"start": v(73.5, 7.02) * mm, "end": v(73.5, -7.04) * mm});
            skLineSegment(sketch, "E71.right", {"start": v(71.92, 7.02) * mm, "end": v(71.92, -7.04) * mm});
            skLineSegment(sketch, "E72.0", {"start": v(73.55, 6.2) * mm, "end": v(71.92, 6.2) * mm});
            skLineSegment(sketch, "E73.1.0.0", {"start": v(73.55, 5.4) * mm, "end": v(71.91, 5.4) * mm});
            skLineSegment(sketch, "E73.2.0.0", {"start": v(73.54, 4.58) * mm, "end": v(71.9, 4.58) * mm});
            skLineSegment(sketch, "E73.3.0.0", {"start": v(73.53, 3.77) * mm, "end": v(71.9, 3.77) * mm});
            skLineSegment(sketch, "E73.4.0.0", {"start": v(73.53, 2.96) * mm, "end": v(71.9, 2.96) * mm});
            skLineSegment(sketch, "E73.5.0.0", {"start": v(73.52, 2.14) * mm, "end": v(71.88, 2.14) * mm});
            skLineSegment(sketch, "E73.6.0.0", {"start": v(73.51, 1.33) * mm, "end": v(71.88, 1.33) * mm});
            skLineSegment(sketch, "E73.7.0.0", {"start": v(73.5, 0.52) * mm, "end": v(71.87, 0.52) * mm});
            skLineSegment(sketch, "E73.8.0.0", {"start": v(73.5, -0.3) * mm, "end": v(71.86, -0.3) * mm});
            skLineSegment(sketch, "E73.9.0.0", {"start": v(73.5, -1.1) * mm, "end": v(71.86, -1.1) * mm});
            skLineSegment(sketch, "E73.10.0.0", {"start": v(73.49, -1.92) * mm, "end": v(71.85, -1.92) * mm});
            skLineSegment(sketch, "E73.11.0.0", {"start": v(73.48, -2.73) * mm, "end": v(71.85, -2.73) * mm});
            skLineSegment(sketch, "E73.12.0.0", {"start": v(73.47, -3.55) * mm, "end": v(71.84, -3.55) * mm});
            skLineSegment(sketch, "E73.13.0.0", {"start": v(73.47, -4.36) * mm, "end": v(71.83, -4.36) * mm});
            skLineSegment(sketch, "E73.14.0.0", {"start": v(73.46, -5.17) * mm, "end": v(71.83, -5.17) * mm});
            skLineSegment(sketch, "E73.15.0.0", {"start": v(73.45, -5.98) * mm, "end": v(71.82, -5.98) * mm});
            skLineSegment(sketch, "E73.direction1", {"start": v(71.92, 6.2) * mm, "end": v(71.91, 5.4) * mm, "construction": true});
            skLineSegment(sketch, "E74", {"start": v(73.5, 7.02) * mm, "end": v(71.92, 6.2) * mm});
            skLineSegment(sketch, "E75", {"start": v(71.92, 6.2) * mm, "end": v(73.55, 5.4) * mm});
            skLineSegment(sketch, "E76", {"start": v(73.55, 5.4) * mm, "end": v(71.9, 4.58) * mm});
            skLineSegment(sketch, "E77", {"start": v(71.9, 4.58) * mm, "end": v(73.53, 3.77) * mm});
            skLineSegment(sketch, "E78", {"start": v(73.53, 3.77) * mm, "end": v(71.92, 2.96) * mm});
            skLineSegment(sketch, "E79", {"start": v(71.92, 2.96) * mm, "end": v(73.52, 2.14) * mm});
            skLineSegment(sketch, "E80", {"start": v(73.52, 2.14) * mm, "end": v(71.92, 1.33) * mm});
            skLineSegment(sketch, "E81", {"start": v(71.92, 1.33) * mm, "end": v(73.49, 0.52) * mm});
            skLineSegment(sketch, "E82", {"start": v(73.49, 0.52) * mm, "end": v(71.92, -0.3) * mm});
            skLineSegment(sketch, "E83", {"start": v(71.92, -0.3) * mm, "end": v(73.49, -1.1) * mm});
            skLineSegment(sketch, "E84", {"start": v(73.49, -1.1) * mm, "end": v(71.9, -1.92) * mm});
            skLineSegment(sketch, "E85", {"start": v(71.9, -1.92) * mm, "end": v(73.48, -2.73) * mm});
            skLineSegment(sketch, "E86", {"start": v(73.48, -2.73) * mm, "end": v(71.92, -3.55) * mm});
            skLineSegment(sketch, "E87", {"start": v(71.92, -3.55) * mm, "end": v(73.49, -4.36) * mm});
            skLineSegment(sketch, "E88", {"start": v(73.49, -4.36) * mm, "end": v(71.92, -5.17) * mm});
            skLineSegment(sketch, "E89", {"start": v(71.92, -5.17) * mm, "end": v(73.45, -5.98) * mm});
            skLineSegment(sketch, "E90", {"start": v(73.45, -5.98) * mm, "end": v(71.92, -7.04) * mm});
            skSolve(sketch);
        }
        {
            var Q0;
            {var subQ0=sQuery(id+"F26.wireOp",EDGE,"E74");Q0=makeQuery(id+"F26.imprint","IMPRINT",FACE,{"disambiguationData":[TD([[makeQuery(id+"F26.imprint","IMPRINT",EDGE,{"derivedFrom":subQ0}),1.0]])]});}
            var Q1;
            {var subQ0=sQuery(id+"F26.wireOp",EDGE,"E72.0");var subQ1=sQuery(id+"F26.wireOp",EDGE,"E71.left");var subQ2=makeQuery(id+"F26.imprint","INTERSECT",VERTEX,{"derivedFrom":[subQ1,subQ0]});Q1=makeQuery(id+"F26.imprint","IMPRINT",FACE,{"disambiguationData":[TD([[makeQuery(id+"F26.imprint","IMPRINT",EDGE,{"disambiguationData":[TD([[subQ2,1.0]])],"derivedFrom":subQ1}),1.0]])]});}
            var Q2;
            {var subQ0=sQuery(id+"F26.wireOp",EDGE,"E73.2.0.0");var subQ1=sQuery(id+"F26.wireOp",EDGE,"E71.left");var subQ2=makeQuery(id+"F26.imprint","INTERSECT",VERTEX,{"derivedFrom":[subQ1,subQ0]});Q2=makeQuery(id+"F26.imprint","IMPRINT",FACE,{"disambiguationData":[TD([[makeQuery(id+"F26.imprint","IMPRINT",EDGE,{"disambiguationData":[TD([[subQ2,-1.0]])],"derivedFrom":subQ1}),1.0]])]});}
            var Q3;
            {var subQ0=sQuery(id+"F26.wireOp",EDGE,"E73.2.0.0");var subQ1=sQuery(id+"F26.wireOp",EDGE,"E71.left");var subQ2=makeQuery(id+"F26.imprint","INTERSECT",VERTEX,{"derivedFrom":[subQ1,subQ0]});Q3=makeQuery(id+"F26.imprint","IMPRINT",FACE,{"disambiguationData":[TD([[makeQuery(id+"F26.imprint","IMPRINT",EDGE,{"disambiguationData":[TD([[subQ2,1.0]])],"derivedFrom":subQ1}),1.0]])]});}
            var Q4;
            {var subQ0=sQuery(id+"F26.wireOp",EDGE,"E73.4.0.0");var subQ1=sQuery(id+"F26.wireOp",EDGE,"E71.left");var subQ2=makeQuery(id+"F26.imprint","INTERSECT",VERTEX,{"derivedFrom":[subQ1,subQ0]});Q4=makeQuery(id+"F26.imprint","IMPRINT",FACE,{"disambiguationData":[TD([[makeQuery(id+"F26.imprint","IMPRINT",EDGE,{"disambiguationData":[TD([[subQ2,-1.0]])],"derivedFrom":subQ1}),1.0]])]});}
            var Q5;
            {var subQ0=sQuery(id+"F26.wireOp",EDGE,"E73.4.0.0");var subQ1=sQuery(id+"F26.wireOp",EDGE,"E71.left");var subQ2=makeQuery(id+"F26.imprint","INTERSECT",VERTEX,{"derivedFrom":[subQ1,subQ0]});Q5=makeQuery(id+"F26.imprint","IMPRINT",FACE,{"disambiguationData":[TD([[makeQuery(id+"F26.imprint","IMPRINT",EDGE,{"disambiguationData":[TD([[subQ2,1.0]])],"derivedFrom":subQ1}),1.0]])]});}
            var Q6;
            {var subQ0=sQuery(id+"F26.wireOp",EDGE,"E73.6.0.0");var subQ1=sQuery(id+"F26.wireOp",EDGE,"E71.left");var subQ2=makeQuery(id+"F26.imprint","INTERSECT",VERTEX,{"derivedFrom":[subQ1,subQ0]});Q6=makeQuery(id+"F26.imprint","IMPRINT",FACE,{"disambiguationData":[TD([[makeQuery(id+"F26.imprint","IMPRINT",EDGE,{"disambiguationData":[TD([[subQ2,-1.0]])],"derivedFrom":subQ1}),1.0]])]});}
            var Q7;
            {var subQ5=sQuery(id+"F26.wireOp",EDGE,"E73.7.0.0");var subQ6=sQuery(id+"F26.wireOp",EDGE,"E71.left");var subQ7=makeQuery(id+"F26.imprint","INTERSECT",VERTEX,{"derivedFrom":[subQ6,subQ5]});Q7=makeQuery(id+"F26.imprint","IMPRINT",FACE,{"disambiguationData":[TD([[makeQuery(id+"F26.imprint","IMPRINT",EDGE,{"disambiguationData":[TD([[subQ7,-1.0]])],"derivedFrom":subQ6}),1.0]])]});}
            var Q8;
            {var subQ5=sQuery(id+"F26.wireOp",EDGE,"E73.8.0.0");var subQ6=sQuery(id+"F26.wireOp",EDGE,"E71.left");var subQ7=makeQuery(id+"F26.imprint","INTERSECT",VERTEX,{"derivedFrom":[subQ6,subQ5]});Q8=makeQuery(id+"F26.imprint","IMPRINT",FACE,{"disambiguationData":[TD([[makeQuery(id+"F26.imprint","IMPRINT",EDGE,{"disambiguationData":[TD([[subQ7,-1.0]])],"derivedFrom":subQ6}),1.0]])]});}
            var Q9;
            {var subQ5=sQuery(id+"F26.wireOp",EDGE,"E73.9.0.0");var subQ7=sQuery(id+"F26.wireOp",EDGE,"E71.left");var subQ8=makeQuery(id+"F26.imprint","INTERSECT",VERTEX,{"derivedFrom":[subQ7,subQ5]});Q9=makeQuery(id+"F26.imprint","IMPRINT",FACE,{"disambiguationData":[TD([[makeQuery(id+"F26.imprint","IMPRINT",EDGE,{"disambiguationData":[TD([[subQ8,-1.0]])],"derivedFrom":subQ7}),1.0]])]});}
            var Q10;
            {var subQ11=sQuery(id+"F26.wireOp",EDGE,"E71.top");Q10=makeQuery(id+"F26.imprint","IMPRINT",FACE,{"disambiguationData":[TD([[makeQuery(id+"F26.imprint","IMPRINT",EDGE,{"derivedFrom":subQ11}),-1.0]])]});}
            extrude(context, id + "F27", {"entities" : qUnion([Q0, Q1, Q2, Q3, Q4, Q5, Q6, Q7, Q8, Q9, Q10]), "operationType" : NewBodyOperationType.REMOVE, "oppositeDirection" : true, "depth" : 25.4 * mm});
        }
    });
